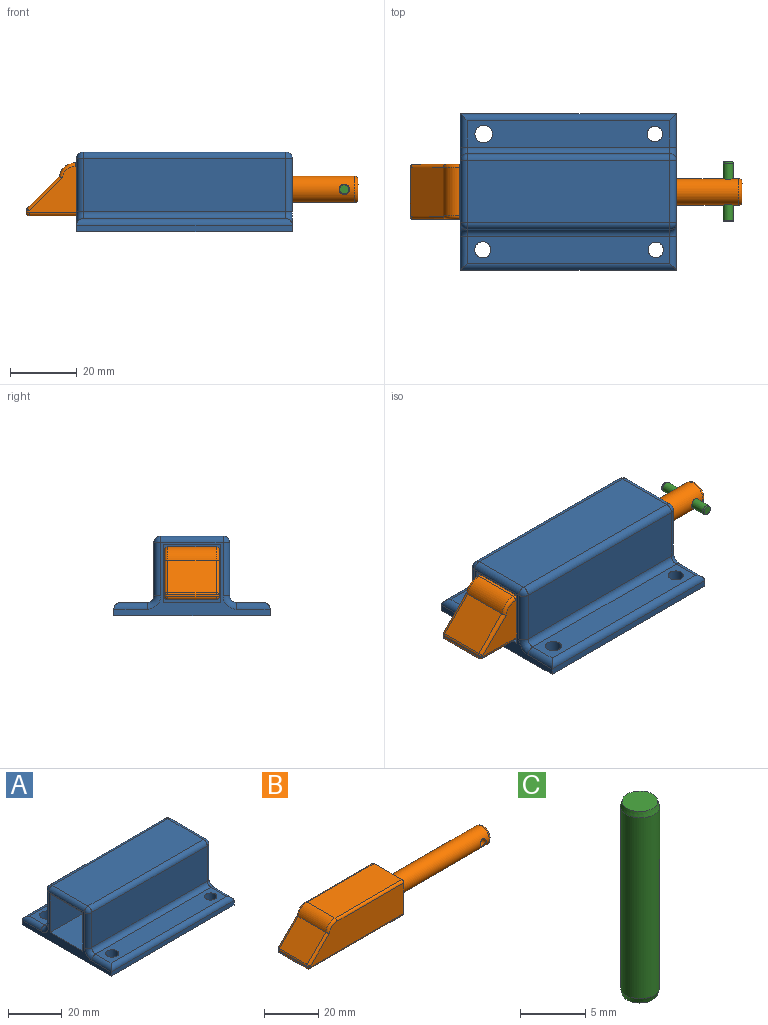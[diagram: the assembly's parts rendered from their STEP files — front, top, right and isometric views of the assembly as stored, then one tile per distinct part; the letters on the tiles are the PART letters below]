
ASSEMBLY  parts=3 mates=2
PART A: 44 faces, bbox 64.9x47x24 mm
  f0: plane 46.98x22mm, normal (-1,0,0), area 175.7mm2, adj f5,f6,f8,f10,f11,f12,f18,f23
  f1: plane 60.92x16mm, normal (0,-1,0), area 974.7mm2, adj f34,f35,f39,f40
  f2: plane 46.98x22mm, normal (1,0,0), area 418.9mm2, adj f5,f6,f8,f19,f20,f22,f25,f30
  f3: plane 60.92x16mm, normal (0,1,0), area 974.7mm2, adj f24,f25,f28,f29
  f4: plane 60.92x18.79mm, normal (0,0,1), area 1144.9mm2, adj f29,f30,f33,f34
  f5: plane 64.92x46.98mm, normal (0,0,-1), area 2976.1mm2, adj f0,f2,f6,f8,f14,f15,f16,f17
  f6: plane 64.92x2mm, normal (0,-1,0), area 129.8mm2, adj f0,f2,f5,f41
  f7: plane 60.92x8.15mm, normal (0,0,1), area 461.2mm2, adj f16,f17,f38,f40,f41,f43
  f8: plane 64.92x2mm, normal (0,1,0), area 129.8mm2, adj f0,f2,f5,f21
  f9: plane 60.92x8.04mm, normal (0,0,1), area 451.1mm2, adj f14,f15,f20,f21,f23,f24
  f10: plane 61x17.55mm, normal (0,1,0), area 1070.4mm2, adj f0,f11,f13,f18
  f11: plane 61x17.15mm, normal (0,0,-1), area 1046.1mm2, adj f0,f10,f12,f13
  f12: plane 61x17.55mm, normal (0,-1,0), area 1070.4mm2, adj f0,f11,f13,f18
  f13: plane 17.55x17.15mm, normal (-1,0,0), area 243.2mm2, adj f10,f11,f12,f18,f19
  f14: cylinder r=2.3mm len=4.61mm, axis (0,0,-1), area 57.9mm2, adj f5,f9
  f15: cylinder r=2.64mm len=5.27mm, axis (0,0,-1), area 66.3mm2, adj f5,f9
  f16: cylinder r=2.43mm len=4.86mm, axis (0,0,-1), area 61.1mm2, adj f5,f7
  f17: cylinder r=2.32mm len=4.64mm, axis (0,0,-1), area 58.3mm2, adj f5,f7
  f18: plane 61x17.15mm, normal (0,0,1), area 1046.1mm2, adj f0,f10,f12,f13
  f19: cylinder r=4.29mm len=8.58mm, axis (1,0,0), area 105.6mm2, adj f2,f13
  f20: cylinder r=2mm len=10.04mm, axis (0,-1,0), area 29.2mm2, adj f2,f9,f21,f22
  f21: cylinder r=2mm len=64.92mm, axis (1,0,0), area 199.4mm2, adj f8,f9,f20,f23
  f22: torus R=4mm, axis (-1,0,0), area 13.5mm2, adj f2,f20,f24,f25
  f23: cylinder r=2mm len=10.04mm, axis (0,1,0), area 29.2mm2, adj f0,f9,f21,f26
  f24: cylinder r=2mm len=60.92mm, axis (-1,0,0), area 191.4mm2, adj f3,f9,f22,f26
  f25: cylinder r=2mm len=16mm, axis (0,0,1), area 50.3mm2, adj f2,f3,f22,f27
  f26: torus R=4mm, axis (-1,0,0), area 13.5mm2, adj f0,f23,f24,f28
  f27: sphere r=2mm, area 6.3mm2, adj f25,f29,f30
  f28: cylinder r=2mm len=16mm, axis (0,0,-1), area 50.3mm2, adj f0,f3,f26,f31
  f29: cylinder r=2mm len=60.92mm, axis (1,0,0), area 191.4mm2, adj f3,f4,f27,f31
  f30: cylinder r=2mm len=18.79mm, axis (0,-1,0), area 59mm2, adj f2,f4,f27,f32
  f31: sphere r=2mm, area 6.3mm2, adj f28,f29,f33
  f32: sphere r=2mm, area 6.3mm2, adj f30,f34,f35
  f33: cylinder r=2mm len=18.79mm, axis (0,1,0), area 59mm2, adj f0,f4,f31,f36
  f34: cylinder r=2mm len=60.92mm, axis (-1,0,0), area 191.4mm2, adj f1,f4,f32,f36
  f35: cylinder r=2mm len=16mm, axis (0,0,-1), area 50.3mm2, adj f1,f2,f32,f37
  f36: sphere r=2mm, area 6.3mm2, adj f33,f34,f39
  f37: torus R=4mm, axis (-1,0,0), area 13.5mm2, adj f2,f35,f38,f40
  f38: cylinder r=2mm len=10.15mm, axis (0,-1,0), area 29.6mm2, adj f2,f7,f37,f41
  f39: cylinder r=2mm len=16mm, axis (0,0,1), area 50.3mm2, adj f0,f1,f36,f42
  f40: cylinder r=2mm len=60.92mm, axis (1,0,0), area 191.4mm2, adj f1,f7,f37,f42
  f41: cylinder r=2mm len=64.92mm, axis (-1,0,0), area 199.4mm2, adj f6,f7,f38,f43
  f42: torus R=4mm, axis (-1,0,0), area 13.5mm2, adj f0,f39,f40,f43
  f43: cylinder r=2mm len=10.15mm, axis (0,1,0), area 29.6mm2, adj f0,f7,f41,f42
PART B: 28 faces, bbox 99.8x16.5x16.3 mm
  f0: cylinder r=3.96mm len=49mm, axis (-1,0,0), area 1204.9mm2, adj f2,f11,f27
  f1: plane 48.81x14.5mm, normal (0,0,-1), area 707.8mm2, adj f2,f8,f13,f20
  f2: plane 16.5x15.9mm, normal (1,0,0), area 212mm2, adj f0,f1,f4,f5,f9,f13,f16,f20
  f3: plane 14.5x0.48mm, normal (-1,0,0), area 7mm2, adj f7,f8,f15,f23
  f4: plane 48.81x13.9mm, normal (0,-1,0), area 591mm2, adj f2,f20,f22,f23,f24,f26
  f5: plane 48.81x13.9mm, normal (0,1,0), area 591mm2, adj f2,f13,f15,f16,f18,f19
  f6: plane 14.5x9.71mm, normal (-0.71,0,0.71), area 199.1mm2, adj f7,f12,f19,f26
  f7: cylinder r=1mm len=14.5mm, axis (0,1,0), area 11.4mm2, adj f3,f6,f17,f25
  f8: cylinder r=1mm len=14.5mm, axis (0,1,0), area 22.8mm2, adj f1,f3,f14,f21
  f9: plane 34.91x14.5mm, normal (0,0,1), area 506.2mm2, adj f2,f12,f16,f22
  f10: plane 5.93x5.93mm, normal (1,0,0), area 27.6mm2, adj f27
  f11: cylinder r=1.57mm len=7.93mm, axis (0,1,0), area 74.9mm2, adj f0
  f12: cylinder r=5mm len=14.5mm, axis (0,-1,0), area 99.3mm2, adj f6,f9,f18,f24
  f13: cylinder r=1mm len=48.81mm, axis (1,0,0), area 76.7mm2, adj f1,f2,f5,f14
  f14: sphere r=1mm, area 1.6mm2, adj f8,f13,f15
  f15: cylinder r=1mm len=1mm, axis (0,0,-1), area 0.8mm2, adj f3,f5,f14,f17
  f16: cylinder r=1mm len=34.91mm, axis (-1,0,0), area 54.8mm2, adj f2,f5,f9,f18
  f17: sphere r=1mm, area 0.8mm2, adj f7,f15,f19
  f18: torus R=4mm, axis (0,-1,0), area 10.1mm2, adj f5,f12,f16,f19
  f19: cylinder r=1mm len=10.64mm, axis (-0.71,0,-0.71), area 21.7mm2, adj f5,f6,f17,f18
  f20: cylinder r=1mm len=48.81mm, axis (-1,0,0), area 76.7mm2, adj f1,f2,f4,f21
  f21: sphere r=1mm, area 1.6mm2, adj f8,f20,f23
  f22: cylinder r=1mm len=34.91mm, axis (1,0,0), area 54.8mm2, adj f2,f4,f9,f24
  f23: cylinder r=1mm len=1mm, axis (0,0,1), area 0.8mm2, adj f3,f4,f21,f25
  f24: torus R=4mm, axis (0,-1,0), area 10.1mm2, adj f4,f12,f22,f26
  f25: sphere r=1mm, area 0.8mm2, adj f7,f23,f26
  f26: cylinder r=1mm len=10.64mm, axis (-0.71,0,-0.71), area 21.7mm2, adj f4,f6,f24,f25
  f27: torus R=2.96mm, axis (1,0,0), area 35.5mm2, adj f0,f10
PART C: 5 faces, bbox 3x3x18 mm
  f0: plane 2.73x2.73mm, normal (0,0,1), area 5.9mm2, adj f1
  f1: cone r=1.37mm half-angle=15deg, axis (0,0,-1), area 4.7mm2, adj f0,f2
  f2: cylinder r=1.5mm len=17mm, axis (0,0,-1), area 160.2mm2, adj f1,f3
  f3: cone r=1.5mm half-angle=15deg, axis (0,0,1), area 4.7mm2, adj f2,f4
  f4: plane 2.73x2.73mm, normal (0,0,-1), area 5.9mm2, adj f3
PLACE A rot(axis=(-0.2,0.48,-0.85),0deg) t=(-2.64,-4.88,-18.75)mm
PLACE B rot(axis=(-0.2,0.48,-0.85),0deg) t=(31.99,26.86,-13.89)mm
PLACE C rot(axis=(-1,0,0),90deg) t=(77.86,18.61,-5.97)mm
MATE fastened C.f1 <-> B.f11  axis (0,1,0) through (77.86,18.61,-5.97)mm
MATE slider B.f0 <-> A.f19  axis (1,0,0) through (80.99,18.61,-5.94)mm
